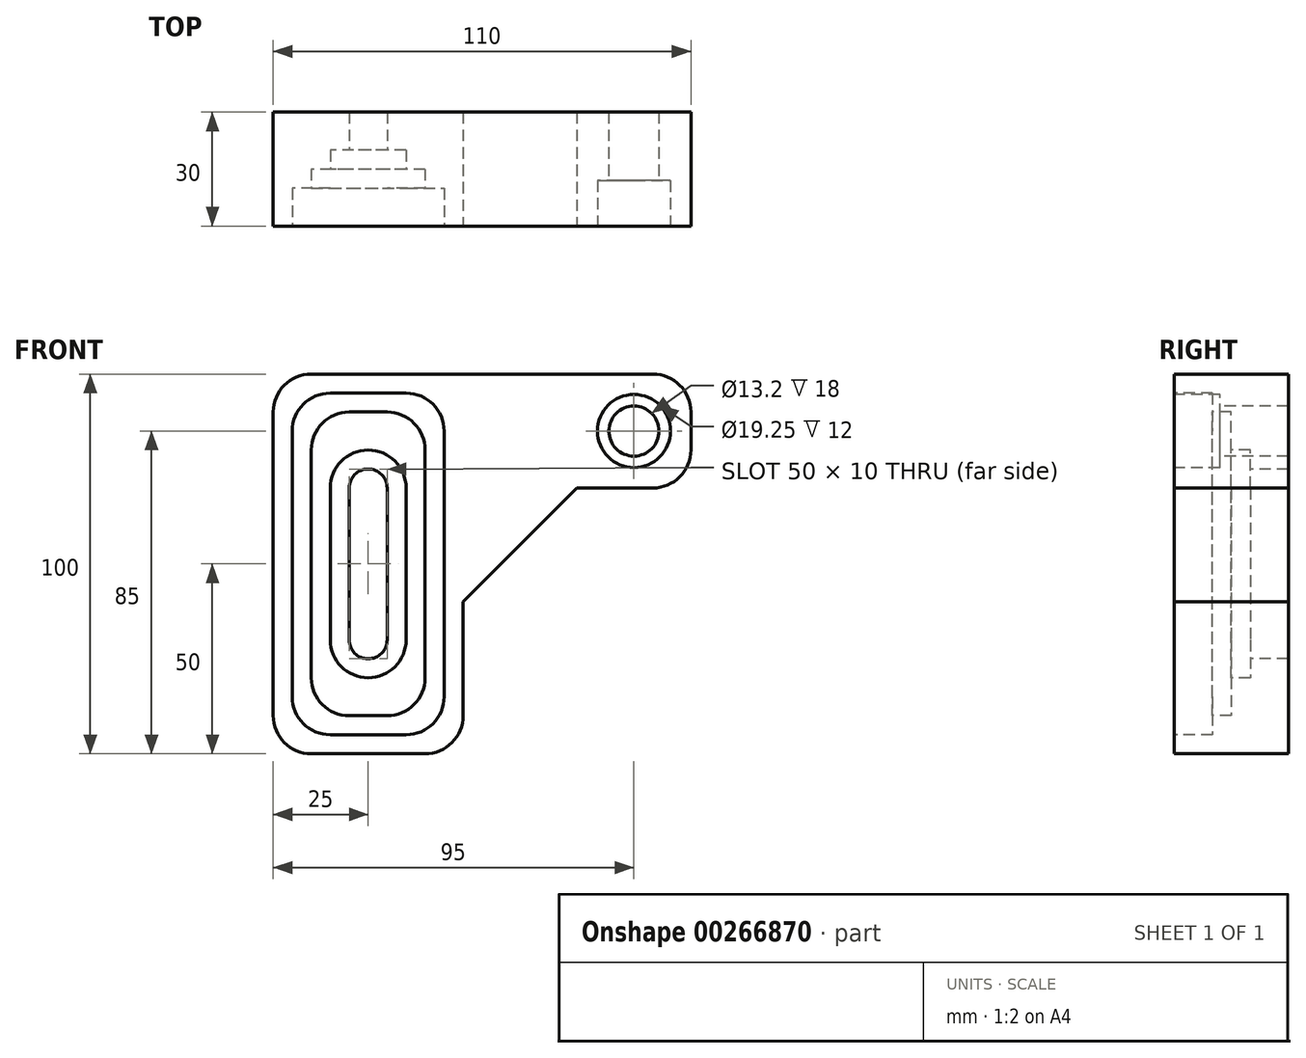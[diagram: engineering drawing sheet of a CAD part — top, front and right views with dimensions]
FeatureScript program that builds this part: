
annotation { "Feature Type Name" : "Feature", "Feature Type Description" : "" }
export const myFeature = defineFeature(function(context is Context, id is Id, definition is map)
    precondition{}
    {
        {
            var Q0;
            Q0=qCreatedBy(makeId("Front.planeOp"),FACE);
            var sketch = newSketch(context, id + "F0", { "sketchPlane" : qUnion([Q0])});
            skLineSegment(sketch, "E0", {"start": v(0, 0) * mm, "end": v(0, -30) * mm});
            skLineSegment(sketch, "E1", {"start": v(-10, -40) * mm, "end": v(-40, -40) * mm});
            skLineSegment(sketch, "E2", {"start": v(-50, -30) * mm, "end": v(-50, 50) * mm});
            skLineSegment(sketch, "E3", {"start": v(-40, 60) * mm, "end": v(50, 60) * mm});
            skLineSegment(sketch, "E4", {"start": v(60, 50) * mm, "end": v(60, 40) * mm});
            skLineSegment(sketch, "E5", {"start": v(50, 30) * mm, "end": v(30, 30) * mm});
            skLineSegment(sketch, "E6", {"start": v(0, 0) * mm, "end": v(30, 30) * mm});
            skLineSegment(sketch, "E7", {"start": v(0, 0) * mm, "end": v(0, 30) * mm, "construction": true});
            skPoint(sketch, "E8.visualSharp", {"position": v(-50, 60) * mm});
            skArc(sketch, "E8.filletArc", {"start": v(-40, 60) * mm, "mid": v(-47.07, 57.07) * mm, "end": v(-50, 50) * mm});
            skPoint(sketch, "E9.visualSharp", {"position": v(60, 60) * mm});
            skArc(sketch, "E9.filletArc", {"start": v(60, 50) * mm, "mid": v(57.07, 57.07) * mm, "end": v(50, 60) * mm});
            skPoint(sketch, "E10.visualSharp", {"position": v(-50, -40) * mm});
            skArc(sketch, "E10.filletArc", {"start": v(-50, -30) * mm, "mid": v(-47.07, -37.07) * mm, "end": v(-40, -40) * mm});
            skPoint(sketch, "E11.visualSharp", {"position": v(0, -40) * mm});
            skArc(sketch, "E11.filletArc", {"start": v(-10, -40) * mm, "mid": v(-2.93, -37.07) * mm, "end": v(0, -30) * mm});
            skPoint(sketch, "E12.visualSharp", {"position": v(60, 30) * mm});
            skArc(sketch, "E12.filletArc", {"start": v(50, 30) * mm, "mid": v(57.07, 32.93) * mm, "end": v(60, 40) * mm});
            skPoint(sketch, "E13", {"position": v(45, 45) * mm});
            skLineSegment(sketch, "E14", {"start": v(-45, 55) * mm, "end": v(-5, 55) * mm});
            skLineSegment(sketch, "E15", {"start": v(-5, 55) * mm, "end": v(-5, -35) * mm});
            skLineSegment(sketch, "E16", {"start": v(-5, -35) * mm, "end": v(-45, -35) * mm});
            skLineSegment(sketch, "E17", {"start": v(-45, -35) * mm, "end": v(-45, 55) * mm});
            skSolve(sketch);
        }
        {
            var Q0;
            Q0=makeQuery(id+"F0.imprint","IMPRINT",FACE,{"disambiguationData":[TD([[makeQuery(id+"F0.imprint","IMPRINT",EDGE,{"derivedFrom":sQuery(id+"F0.wireOp",EDGE,"E0")}),-1.0]])]});
            var Q1;
            Q1=makeQuery(id+"F0.imprint","IMPRINT",FACE,{"disambiguationData":[TD([[makeQuery(id+"F0.imprint","IMPRINT",EDGE,{"derivedFrom":sQuery(id+"F0.wireOp",EDGE,"E14")}),-1.0]])]});
            extrude(context, id + "F1", {"entities" : qUnion([Q0, Q1]), "oppositeDirection" : true, "depth" : 30 * mm});
        }
        {
            var Q0;
            Q0=makeQuery(id+"F0.imprint","IMPRINT",FACE,{"disambiguationData":[TD([[makeQuery(id+"F0.imprint","IMPRINT",EDGE,{"derivedFrom":sQuery(id+"F0.wireOp",EDGE,"E14")}),-1.0]])]});
            var sketch = newSketch(context, id + "F2", { "sketchPlane" : qUnion([Q0])});
            skLineSegment(sketch, "E18.0.0", {"start": v(-45, 45) * mm, "end": v(-45, -25) * mm});
            skLineSegment(sketch, "E18.0.1", {"start": v(-35, -35) * mm, "end": v(-15, -35) * mm});
            skLineSegment(sketch, "E18.0.2", {"start": v(-5, -25) * mm, "end": v(-5, 45) * mm});
            skLineSegment(sketch, "E18.0.3", {"start": v(-15, 55) * mm, "end": v(-35, 55) * mm});
            skLineSegment(sketch, "E19", {"start": v(-45, 10) * mm, "end": v(-5, 10) * mm, "construction": true});
            skLineSegment(sketch, "E20", {"start": v(-25, 30) * mm, "end": v(-25, -10) * mm});
            skPoint(sketch, "E20.startSnap0", {"position": v(-25, 10) * mm});
            skArc(sketch, "E21", {"start": v(-20, 30) * mm, "mid": v(-25, 35) * mm, "end": v(-30, 30) * mm});
            skLineSegment(sketch, "E22", {"start": v(-20, 30) * mm, "end": v(-20, -10) * mm});
            skLineSegment(sketch, "E23", {"start": v(-30, 30) * mm, "end": v(-30, -10) * mm});
            skArc(sketch, "E24", {"start": v(-30, -10) * mm, "mid": v(-25, -15) * mm, "end": v(-20, -10) * mm});
            skArc(sketch, "E25", {"start": v(-15, 30) * mm, "mid": v(-25, 40) * mm, "end": v(-35, 30) * mm});
            skArc(sketch, "E26", {"start": v(-35, -10) * mm, "mid": v(-25, -20) * mm, "end": v(-15, -10) * mm});
            skLineSegment(sketch, "E27", {"start": v(-35, 30) * mm, "end": v(-35, -10) * mm});
            skLineSegment(sketch, "E28", {"start": v(-15, 30) * mm, "end": v(-15, -10) * mm});
            skLineSegment(sketch, "E29.0", {"start": v(-20, 50) * mm, "end": v(-30, 50) * mm});
            skLineSegment(sketch, "E29.1", {"start": v(-10, -20) * mm, "end": v(-10, 40) * mm});
            skLineSegment(sketch, "E29.2", {"start": v(-30, -30) * mm, "end": v(-20, -30) * mm});
            skLineSegment(sketch, "E29.3", {"start": v(-40, 40) * mm, "end": v(-40, -20) * mm});
            skPoint(sketch, "E30.visualSharp", {"position": v(-45, 55) * mm});
            skArc(sketch, "E30.filletArc", {"start": v(-35, 55) * mm, "mid": v(-42.07, 52.07) * mm, "end": v(-45, 45) * mm});
            skPoint(sketch, "E31.visualSharp", {"position": v(-40, 50) * mm});
            skArc(sketch, "E31.filletArc", {"start": v(-30, 50) * mm, "mid": v(-37.07, 47.07) * mm, "end": v(-40, 40) * mm});
            skPoint(sketch, "E32.visualSharp", {"position": v(-5, 55) * mm});
            skArc(sketch, "E32.filletArc", {"start": v(-5, 45) * mm, "mid": v(-7.93, 52.07) * mm, "end": v(-15, 55) * mm});
            skPoint(sketch, "E33.visualSharp", {"position": v(-10, 50) * mm});
            skArc(sketch, "E33.filletArc", {"start": v(-10, 40) * mm, "mid": v(-12.93, 47.07) * mm, "end": v(-20, 50) * mm});
            skPoint(sketch, "E34.visualSharp", {"position": v(-5, -35) * mm});
            skArc(sketch, "E34.filletArc", {"start": v(-15, -35) * mm, "mid": v(-7.93, -32.07) * mm, "end": v(-5, -25) * mm});
            skPoint(sketch, "E35.visualSharp", {"position": v(-10, -30) * mm});
            skArc(sketch, "E35.filletArc", {"start": v(-20, -30) * mm, "mid": v(-12.93, -27.07) * mm, "end": v(-10, -20) * mm});
            skPoint(sketch, "E36.visualSharp", {"position": v(-40, -30) * mm});
            skArc(sketch, "E36.filletArc", {"start": v(-40, -20) * mm, "mid": v(-37.07, -27.07) * mm, "end": v(-30, -30) * mm});
            skPoint(sketch, "E37.visualSharp", {"position": v(-45, -35) * mm});
            skArc(sketch, "E37.filletArc", {"start": v(-45, -25) * mm, "mid": v(-42.07, -32.07) * mm, "end": v(-35, -35) * mm});
            skSolve(sketch);
        }
        {
            var Q0;
            Q0=makeQuery(id+"F2.imprint","IMPRINT",FACE,{"disambiguationData":[TD([[makeQuery(id+"F2.imprint","IMPRINT",EDGE,{"derivedFrom":sQuery(id+"F2.wireOp",EDGE,"E21")}),-1.0]])]});
            extrude(context, id + "F3", {"entities" : qUnion([Q0]), "operationType" : NewBodyOperationType.REMOVE, "oppositeDirection" : true, "depth" : 20 * mm});
        }
        {
            var Q0;
            Q0=makeQuery(id+"F2.imprint","IMPRINT",FACE,{"disambiguationData":[TD([[makeQuery(id+"F2.imprint","IMPRINT",EDGE,{"derivedFrom":sQuery(id+"F2.wireOp",EDGE,"E21")}),1.0]])]});
            extrude(context, id + "F4", {"entities" : qUnion([Q0]), "operationType" : NewBodyOperationType.REMOVE, "oppositeDirection" : true, "depth" : 30 * mm});
        }
        {
            var Q0;
            Q0=sQuery(id+"F0.wireOp",VERTEX,"E13");
            var Q1;
            Q1=makeQuery(id+"F1.opExtrude","SWEPT_BODY",BODY,{"disambiguationData":[OSD([sQuery(id+"F0.wireOp",EDGE,"E0"),sQuery(id+"F0.wireOp",EDGE,"E1"),sQuery(id+"F0.wireOp",EDGE,"E2"),sQuery(id+"F0.wireOp",EDGE,"E3"),sQuery(id+"F0.wireOp",EDGE,"E4"),sQuery(id+"F0.wireOp",EDGE,"E5"),sQuery(id+"F0.wireOp",EDGE,"E6"),sQuery(id+"F0.wireOp",EDGE,"E8.filletArc"),sQuery(id+"F0.wireOp",EDGE,"E9.filletArc"),sQuery(id+"F0.wireOp",EDGE,"E10.filletArc"),sQuery(id+"F0.wireOp",EDGE,"E11.filletArc"),sQuery(id+"F0.wireOp",EDGE,"E12.filletArc")])]});
            hole(context, id + "F5", {"style" : HoleStyle.C_BORE, "endStyle" : HoleEndStyle.THROUGH, "standardTappedOrClearance" : lookupTablePath({ "standard" : "ISO", "fit" : "Normal", "size" : "M12", "type" : "Clearance" }), "standardBlindInLast" : lookupTablePath({ "fit" : "Standard", "standard" : "ISO", "size" : "M12", "type" : "Clearance" }), "holeDiameter" : 13.2 * mm, "cBoreDiameter" : 19.25 * mm, "cBoreDepth" : 12 * mm, "tappedDepth" : 12 * mm, "tapClearance" : 3, "locations" : qUnion([Q0]), "scope" : qUnion([Q1])});
        }
        {
            var Q0;
            Q0=makeQuery(id+"F2.imprint","IMPRINT",FACE,{"disambiguationData":[TD([[makeQuery(id+"F2.imprint","IMPRINT",EDGE,{"derivedFrom":sQuery(id+"F2.wireOp",EDGE,"E18.0.0")}),-1.0]])]});
            extrude(context, id + "F6", {"entities" : qUnion([Q0]), "operationType" : NewBodyOperationType.REMOVE, "oppositeDirection" : true, "depth" : 10 * mm});
        }
        {
            var Q0;
            {var subQ0=makeQuery(id+"F3.opExtrude","SWEPT_FACE",FACE,{"disambiguationData":[OSD([sQuery(id+"F2.wireOp",EDGE,"E25")])]});var subQ4=sQuery(id+"F0.wireOp",EDGE,"E10.filletArc");var subQ5=sQuery(id+"F0.wireOp",EDGE,"E8.filletArc");var subQ6=sQuery(id+"F0.wireOp",EDGE,"E6");var subQ7=sQuery(id+"F0.wireOp",EDGE,"E5");var subQ8=sQuery(id+"F0.wireOp",EDGE,"E4");var subQ9=sQuery(id+"F0.wireOp",EDGE,"E0");var subQ10=sQuery(id+"F0.wireOp",EDGE,"E9.filletArc");var subQ11=sQuery(id+"F0.wireOp",EDGE,"E1");var subQ12=sQuery(id+"F0.wireOp",EDGE,"E2");var subQ13=sQuery(id+"F0.wireOp",EDGE,"E3");var subQ14=sQuery(id+"F0.wireOp",EDGE,"E11.filletArc");var subQ15=sQuery(id+"F0.wireOp",EDGE,"E12.filletArc");Q0=makeQuery(id+"F6.boolean.opBoolean","SPLIT",FACE,{"disambiguationData":[TD([makeQuery(id+"F3.boolean.opBoolean","COPY",FACE,{"derivedFrom":subQ0})])],"derivedFrom":makeQuery(id+"F3.boolean.opBoolean","SPLIT",FACE,{"disambiguationData":[TD([makeQuery(id+"F1.opExtrude","SWEPT_FACE",FACE,{"disambiguationData":[OSD([subQ9])]})])],"derivedFrom":makeQuery(id+"F1.opExtrude","CAP_FACE",FACE,{"disambiguationData":[OSD([subQ9,subQ11,subQ12,subQ13,subQ8,subQ7,subQ6,subQ5,subQ10,subQ4,subQ14,subQ15])],"isStart":true})})});}
            extrude(context, id + "F7", {"entities" : qUnion([Q0]), "operationType" : NewBodyOperationType.REMOVE, "oppositeDirection" : true, "depth" : 15 * mm});
        }
    });
